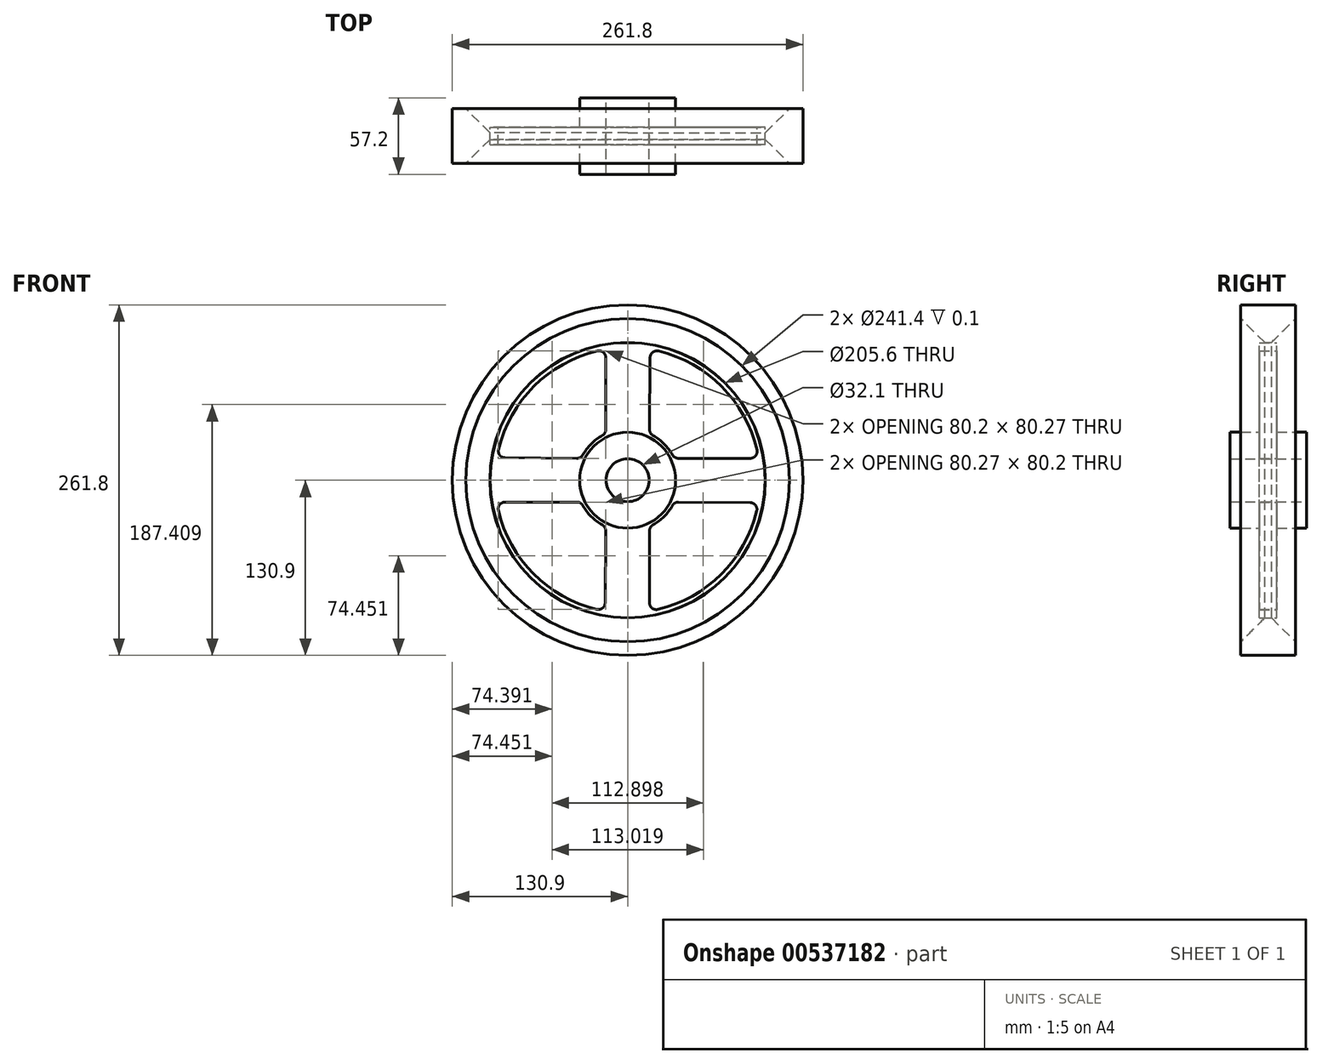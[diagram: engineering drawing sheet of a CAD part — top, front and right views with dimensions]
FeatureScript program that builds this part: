
annotation { "Feature Type Name" : "Feature", "Feature Type Description" : "" }
export const myFeature = defineFeature(function(context is Context, id is Id, definition is map)
    precondition{}
    {
        {
            var Q0;
            Q0=qCreatedBy(makeId("Front.planeOp"),FACE);
            var sketch = newSketch(context, id + "F0", { "sketchPlane" : qUnion([Q0])});
            skCircle(sketch, "E0", {"center": v(0, 0) * mm, "radius": 35.8 * mm});
            skCircle(sketch, "E1", {"center": v(0, 0) * mm, "radius": 16.05 * mm});
            skArc(sketch, "E2", {"start": v(-18.9, 33.43) * mm, "mid": v(-27.14, 27.16) * mm, "end": v(-33.42, 18.91) * mm});
            skCircle(sketch, "E3", {"center": v(0, 0) * mm, "radius": 102.7 * mm});
            skArc(sketch, "E4", {"start": v(-96.52, -22.48) * mm, "mid": v(-70.23, -69.91) * mm, "end": v(-22.92, -96.41) * mm});
            skArc(sketch, "E5.trimOffspring", {"start": v(33.43, 18.9) * mm, "mid": v(27.16, 27.14) * mm, "end": v(18.91, 33.42) * mm});
            skArc(sketch, "E6.trimOffspring", {"start": v(-33.43, -18.9) * mm, "mid": v(-27.16, -27.14) * mm, "end": v(-18.91, -33.42) * mm});
            skArc(sketch, "E7.trimOffspring", {"start": v(18.9, -33.43) * mm, "mid": v(27.14, -27.16) * mm, "end": v(33.42, -18.91) * mm});
            skArc(sketch, "E8.trimOffspring", {"start": v(96.52, 22.48) * mm, "mid": v(70.23, 69.91) * mm, "end": v(22.92, 96.41) * mm});
            skArc(sketch, "E9.trimOffspring", {"start": v(22.48, -96.52) * mm, "mid": v(69.91, -70.23) * mm, "end": v(96.41, -22.92) * mm});
            skArc(sketch, "E10.trimOffspring", {"start": v(-22.48, 96.52) * mm, "mid": v(-69.91, 70.23) * mm, "end": v(-96.41, 22.92) * mm});
            skLineSegment(sketch, "E11", {"start": v(-91.65, -16.35) * mm, "end": v(-37.79, -16.35) * mm});
            skLineSegment(sketch, "E12", {"start": v(-16.77, -91.58) * mm, "end": v(-16.37, -37.8) * mm});
            skLineSegment(sketch, "E13", {"start": v(16.35, -91.65) * mm, "end": v(16.35, -37.79) * mm});
            skLineSegment(sketch, "E14", {"start": v(37.8, -16.37) * mm, "end": v(91.58, -16.77) * mm});
            skLineSegment(sketch, "E15", {"start": v(37.79, 16.35) * mm, "end": v(91.65, 16.35) * mm});
            skLineSegment(sketch, "E16", {"start": v(16.37, 37.8) * mm, "end": v(16.77, 91.58) * mm});
            skLineSegment(sketch, "E17", {"start": v(-16.35, 91.65) * mm, "end": v(-16.35, 37.79) * mm});
            skLineSegment(sketch, "E18", {"start": v(-91.58, 16.77) * mm, "end": v(-37.8, 16.37) * mm});
            skPoint(sketch, "E19.visualSharp", {"position": v(-97.66, 16.81) * mm});
            skArc(sketch, "E19.filletArc", {"start": v(-96.41, 22.92) * mm, "mid": v(-95.48, 18.68) * mm, "end": v(-91.58, 16.77) * mm});
            skPoint(sketch, "E20.visualSharp", {"position": v(-16.35, 97.74) * mm});
            skArc(sketch, "E20.filletArc", {"start": v(-16.35, 91.65) * mm, "mid": v(-18.24, 95.56) * mm, "end": v(-22.48, 96.52) * mm});
            skPoint(sketch, "E21.visualSharp", {"position": v(-34.75, 16.35) * mm});
            skArc(sketch, "E21.filletArc", {"start": v(-37.8, 16.37) * mm, "mid": v(-35.27, 17.04) * mm, "end": v(-33.42, 18.91) * mm});
            skPoint(sketch, "E22.visualSharp", {"position": v(-16.35, 34.75) * mm});
            skArc(sketch, "E22.filletArc", {"start": v(-18.9, 33.43) * mm, "mid": v(-17.03, 35.27) * mm, "end": v(-16.35, 37.79) * mm});
            skPoint(sketch, "E23.visualSharp", {"position": v(16.81, 97.66) * mm});
            skArc(sketch, "E23.filletArc", {"start": v(22.92, 96.41) * mm, "mid": v(18.68, 95.48) * mm, "end": v(16.77, 91.58) * mm});
            skPoint(sketch, "E24.visualSharp", {"position": v(16.35, 34.75) * mm});
            skArc(sketch, "E24.filletArc", {"start": v(16.37, 37.8) * mm, "mid": v(17.04, 35.27) * mm, "end": v(18.91, 33.42) * mm});
            skPoint(sketch, "E25.visualSharp", {"position": v(34.75, 16.35) * mm});
            skArc(sketch, "E25.filletArc", {"start": v(33.43, 18.9) * mm, "mid": v(35.27, 17.03) * mm, "end": v(37.79, 16.35) * mm});
            skPoint(sketch, "E26.visualSharp", {"position": v(97.74, 16.35) * mm});
            skArc(sketch, "E26.filletArc", {"start": v(91.65, 16.35) * mm, "mid": v(95.56, 18.24) * mm, "end": v(96.52, 22.48) * mm});
            skPoint(sketch, "E27.visualSharp", {"position": v(34.75, -16.35) * mm});
            skArc(sketch, "E27.filletArc", {"start": v(37.8, -16.37) * mm, "mid": v(35.27, -17.04) * mm, "end": v(33.42, -18.91) * mm});
            skPoint(sketch, "E28.visualSharp", {"position": v(97.66, -16.81) * mm});
            skArc(sketch, "E28.filletArc", {"start": v(96.41, -22.92) * mm, "mid": v(95.48, -18.68) * mm, "end": v(91.58, -16.77) * mm});
            skPoint(sketch, "E29.visualSharp", {"position": v(16.35, -97.74) * mm});
            skArc(sketch, "E29.filletArc", {"start": v(16.35, -91.65) * mm, "mid": v(18.24, -95.56) * mm, "end": v(22.48, -96.52) * mm});
            skPoint(sketch, "E30.visualSharp", {"position": v(16.35, -34.75) * mm});
            skArc(sketch, "E30.filletArc", {"start": v(18.9, -33.43) * mm, "mid": v(17.03, -35.27) * mm, "end": v(16.35, -37.79) * mm});
            skPoint(sketch, "E31.visualSharp", {"position": v(-16.35, -34.75) * mm});
            skArc(sketch, "E31.filletArc", {"start": v(-16.37, -37.8) * mm, "mid": v(-17.04, -35.27) * mm, "end": v(-18.91, -33.42) * mm});
            skPoint(sketch, "E32.visualSharp", {"position": v(-16.81, -97.66) * mm});
            skArc(sketch, "E32.filletArc", {"start": v(-22.92, -96.41) * mm, "mid": v(-18.68, -95.48) * mm, "end": v(-16.77, -91.58) * mm});
            skPoint(sketch, "E33.visualSharp", {"position": v(-34.75, -16.35) * mm});
            skArc(sketch, "E33.filletArc", {"start": v(-33.43, -18.9) * mm, "mid": v(-35.27, -17.03) * mm, "end": v(-37.79, -16.35) * mm});
            skPoint(sketch, "E34.visualSharp", {"position": v(-97.74, -16.35) * mm});
            skArc(sketch, "E34.filletArc", {"start": v(-91.65, -16.35) * mm, "mid": v(-95.56, -18.24) * mm, "end": v(-96.52, -22.48) * mm});
            skSolve(sketch);
        }
        {
            var Q0;
            Q0 = qSketchRegion(id + "F0", true);
            extrude(context, id + "F1", {"entities" : qUnion([Q0]), "endBound" : BoundingType.SYMMETRIC, "depth" : 13 * mm, "offsetDistance" : 25 * mm});
        }
        {
            var Q0;
            Q0=makeQuery(id+"F0.imprint","IMPRINT",FACE,{"disambiguationData":[TD([[makeQuery(id+"F0.imprint","IMPRINT",EDGE,{"derivedFrom":sQuery(id+"F0.wireOp",EDGE,"E0")}),1.0]])]});
            extrude(context, id + "F2", {"entities" : qUnion([Q0]), "operationType" : NewBodyOperationType.ADD, "endBound" : BoundingType.SYMMETRIC, "depth" : 57.2 * mm, "offsetDistance" : 25 * mm});
        }
        {
            var Q0;
            Q0=qCreatedBy(makeId("Front.planeOp"),FACE);
            var sketch = newSketch(context, id + "F3", { "sketchPlane" : qUnion([Q0])});
            skCircle(sketch, "E35", {"center": v(0, 0) * mm, "radius": 120.7 * mm});
            skCircle(sketch, "E36", {"center": v(0, 0) * mm, "radius": 39.28 * mm});
            skCircle(sketch, "E37", {"center": v(0, 0) * mm, "radius": 130.9 * mm});
            skCircle(sketch, "E38", {"center": v(0, 0) * mm, "radius": 102.8 * mm});
            skSolve(sketch);
        }
        {
            var Q0;
            Q0=makeQuery(id+"F3.imprint","IMPRINT",FACE,{"disambiguationData":[TD([[makeQuery(id+"F3.imprint","IMPRINT",EDGE,{"derivedFrom":sQuery(id+"F3.wireOp",EDGE,"E35")}),1.0]])]});
            extrude(context, id + "F4", {"entities" : qUnion([Q0]), "endBound" : BoundingType.SYMMETRIC, "depth" : 41 * mm, "offsetDistance" : 25 * mm});
        }
        {
            var Q0;
            Q0=makeQuery(id+"F4.opExtrude","SWEPT_FACE",FACE,{"disambiguationData":[OSD([sQuery(id+"F3.wireOp",EDGE,"E38")])]});
            chamfer(context, id + "F5", {"entities" : qUnion([Q0]), "width" : 18 * mm, "tangentPropagation" : true});
        }
        {
            var Q0;
            Q0=makeQuery(id+"F3.imprint","IMPRINT",FACE,{"disambiguationData":[TD([[makeQuery(id+"F3.imprint","IMPRINT",EDGE,{"derivedFrom":sQuery(id+"F3.wireOp",EDGE,"E35")}),-1.0]])]});
            extrude(context, id + "F6", {"entities" : qUnion([Q0]), "operationType" : NewBodyOperationType.ADD, "endBound" : BoundingType.SYMMETRIC, "depth" : 41 * mm, "offsetDistance" : 25 * mm});
        }
    });
